annotation { "Feature Type Name" : "Feature", "Feature Type Description" : "" }
export const myFeature = defineFeature(function(context is Context, id is Id, definition is map)
    precondition{}
    {
        {
            var Q0;
            Q0=qCreatedBy(makeId("Top.planeOp"),FACE);
            var sketch = newSketch(context, id + "F0", { "sketchPlane" : qUnion([Q0])});
            skLineSegment(sketch, "E0", {"start": v(0, 0) * mm, "end": v(-38.42, 0) * mm});
            skLineSegment(sketch, "E1", {"start": v(-38.42, 0) * mm, "end": v(-32.56, -66.93) * mm});
            skLineSegment(sketch, "E2", {"start": v(-22.44, -76.2) * mm, "end": v(0, -76.2) * mm});
            skLineSegment(sketch, "E3", {"start": v(0, -76.2) * mm, "end": v(0, 0) * mm});
            skPoint(sketch, "E4.visualSharp", {"position": v(-31.75, -76.2) * mm});
            skArc(sketch, "E4.filletArc", {"start": v(-32.56, -66.93) * mm, "mid": v(-29.3, -73.53) * mm, "end": v(-22.44, -76.2) * mm});
            skSolve(sketch);
        }
        {
            var Q0;
            Q0=makeQuery(id+"F0.imprint","IMPRINT",FACE,{"disambiguationData":[TD([[makeQuery(id+"F0.imprint","IMPRINT",EDGE,{"derivedFrom":sQuery(id+"F0.wireOp",EDGE,"E0")}),1.0]])]});
            var Q1;
            Q1=sQuery(id+"F0.wireOp",EDGE,"E3");
            revolve(context, id + "F1", {"surfaceOperationType" : NewSurfaceOperationType.NEW, "entities" : qUnion([Q0]), "axis" : qUnion([Q1]), "revolveType" : RevolveType.FULL});
        }
        {
            var Q0;
            Q0=makeQuery(id+"F1.opRevolve","SWEPT_EDGE",EDGE,{"disambiguationData":[OSD([sQuery(id+"F0.wireOp",EDGE,"E0"),sQuery(id+"F0.wireOp",EDGE,"E1")])]});
            var Q1;
            Q1=makeQuery(id+"F3.opShell","OFFSET_EDGE",EDGE,{"disambiguationData":[OSD([sQuery(id+"F0.wireOp",EDGE,"E0"),sQuery(id+"F0.wireOp",EDGE,"E1")])]});
            fillet(context, id + "F2", {"entities" : qUnion([Q0, Q1]), "radius" : 1.27 * mm, "tangentPropagation" : true, "allowEdgeOverflow" : false});
        }
        {
            var Q0;
            Q0=makeQuery(id+"F1.opRevolve","SWEPT_FACE",FACE,{"disambiguationData":[OSD([sQuery(id+"F0.wireOp",EDGE,"E0")])]});
            shell(context, id + "F3", {"entities" : qUnion([Q0]), "thickness" : 2.54 * mm});
        }
        {
            var Q0;
            Q0=qCreatedBy(makeId("Top.planeOp"),FACE);
            var sketch = newSketch(context, id + "F4", { "sketchPlane" : qUnion([Q0])});
            skArc(sketch, "E5", {"start": v(-13.78, -14.23) * mm, "mid": v(-23.6, -20.04) * mm, "end": v(-13.78, -25.85) * mm});
            skArc(sketch, "E6", {"start": v(-12.2, -12.87) * mm, "mid": v(-25.58, -20.04) * mm, "end": v(-12.2, -27.2) * mm});
            skArc(sketch, "E7", {"start": v(-12.2, -15.44) * mm, "mid": v(-14.05, -20.04) * mm, "end": v(-12.2, -24.64) * mm});
            skArc(sketch, "E8", {"start": v(-13.78, -14.23) * mm, "mid": v(-16.03, -20.04) * mm, "end": v(-13.78, -25.85) * mm});
            skArc(sketch, "E9", {"start": v(-1, -25.78) * mm, "mid": v(2.24, -26.67) * mm, "end": v(5.5, -25.85) * mm});
            skArc(sketch, "E10", {"start": v(-2.56, -27.14) * mm, "mid": v(2.25, -28.65) * mm, "end": v(7.08, -27.2) * mm});
            skArc(sketch, "E11", {"start": v(7.08, -15.44) * mm, "mid": v(5.23, -20.04) * mm, "end": v(7.08, -24.64) * mm});
            skArc(sketch, "E12", {"start": v(5.5, -14.23) * mm, "mid": v(3.25, -20.04) * mm, "end": v(5.5, -25.85) * mm});
            skArc(sketch, "E13.trimOffspring", {"start": v(-12.2, -24.64) * mm, "mid": v(-10.34, -20.04) * mm, "end": v(-12.2, -15.44) * mm});
            skArc(sketch, "E14.trimOffspring", {"start": v(-10.62, -25.85) * mm, "mid": v(-7.35, -26.67) * mm, "end": v(-4.1, -25.78) * mm});
            skArc(sketch, "E15.trimOffspring", {"start": v(-12.2, -27.2) * mm, "mid": v(-7.37, -28.65) * mm, "end": v(-2.56, -27.14) * mm});
            skArc(sketch, "E16.trimOffspring", {"start": v(-10.62, -25.85) * mm, "mid": v(-8.36, -20.04) * mm, "end": v(-10.62, -14.23) * mm});
            skArc(sketch, "E17.trimOffspring", {"start": v(-2.56, -24.54) * mm, "mid": v(-0.8, -20.04) * mm, "end": v(-2.56, -15.53) * mm});
            skArc(sketch, "E18.trimOffspring", {"start": v(-1, -25.78) * mm, "mid": v(1.19, -20.04) * mm, "end": v(-1, -14.3) * mm});
            skArc(sketch, "E19.trimOffspring", {"start": v(-4.1, -14.3) * mm, "mid": v(-6.3, -20.04) * mm, "end": v(-4.1, -25.78) * mm});
            skArc(sketch, "E20.trimOffspring", {"start": v(-4.1, -14.3) * mm, "mid": v(-7.35, -13.4) * mm, "end": v(-10.62, -14.23) * mm});
            skArc(sketch, "E21.trimOffspring", {"start": v(-2.56, -15.53) * mm, "mid": v(-4.32, -20.04) * mm, "end": v(-2.56, -24.54) * mm});
            skArc(sketch, "E22.trimOffspring", {"start": v(-2.56, -12.93) * mm, "mid": v(-7.37, -11.43) * mm, "end": v(-12.2, -12.87) * mm});
            skArc(sketch, "E23.trimOffspring", {"start": v(5.5, -14.23) * mm, "mid": v(2.24, -13.4) * mm, "end": v(-1, -14.3) * mm});
            skArc(sketch, "E24.trimOffspring", {"start": v(7.08, -12.87) * mm, "mid": v(2.25, -11.43) * mm, "end": v(-2.56, -12.93) * mm});
            skArc(sketch, "E25.trimOffspring", {"start": v(8.66, -25.85) * mm, "mid": v(18.49, -20.04) * mm, "end": v(8.66, -14.23) * mm});
            skArc(sketch, "E26.trimOffspring", {"start": v(7.08, -24.64) * mm, "mid": v(8.94, -20.04) * mm, "end": v(7.08, -15.44) * mm});
            skArc(sketch, "E27.trimOffspring", {"start": v(8.66, -25.85) * mm, "mid": v(10.92, -20.04) * mm, "end": v(8.66, -14.23) * mm});
            skArc(sketch, "E28.trimOffspring", {"start": v(7.08, -27.2) * mm, "mid": v(20.47, -20.04) * mm, "end": v(7.08, -12.87) * mm});
            skSolve(sketch);
        }
        {
            var Q0;
            Q0=makeQuery(id+"F4.imprint","IMPRINT",FACE,{"disambiguationData":[TD([[makeQuery(id+"F4.imprint","IMPRINT",EDGE,{"derivedFrom":sQuery(id+"F4.wireOp",EDGE,"E5")}),-1.0]])]});
            var Q1;
            Q1=sQuery(id+"F4.wireOp",EDGE,"E6");
            var Q2;
            Q2=sQuery(id+"F4.wireOp",EDGE,"E5");
            var Q3;
            Q3=sQuery(id+"F4.wireOp",EDGE,"E8");
            var Q4;
            Q4=sQuery(id+"F4.wireOp",EDGE,"E7");
            var Q5;
            Q5=sQuery(id+"F4.wireOp",EDGE,"E13.trimOffspring");
            var Q6;
            Q6=sQuery(id+"F4.wireOp",EDGE,"E16.trimOffspring");
            var Q7;
            Q7=sQuery(id+"F4.wireOp",EDGE,"E20.trimOffspring");
            var Q8;
            Q8=sQuery(id+"F4.wireOp",EDGE,"E22.trimOffspring");
            var Q9;
            Q9=sQuery(id+"F4.wireOp",EDGE,"E19.trimOffspring");
            var Q10;
            Q10=sQuery(id+"F4.wireOp",EDGE,"E21.trimOffspring");
            var Q11;
            Q11=sQuery(id+"F4.wireOp",EDGE,"E14.trimOffspring");
            var Q12;
            Q12=sQuery(id+"F4.wireOp",EDGE,"E15.trimOffspring");
            var Q13;
            Q13=sQuery(id+"F4.wireOp",EDGE,"E10");
            var Q14;
            Q14=sQuery(id+"F4.wireOp",EDGE,"E9");
            var Q15;
            Q15=sQuery(id+"F4.wireOp",EDGE,"E18.trimOffspring");
            var Q16;
            Q16=sQuery(id+"F4.wireOp",EDGE,"E17.trimOffspring");
            var Q17;
            Q17=sQuery(id+"F4.wireOp",EDGE,"E23.trimOffspring");
            var Q18;
            Q18=sQuery(id+"F4.wireOp",EDGE,"E24.trimOffspring");
            var Q19;
            Q19=sQuery(id+"F4.wireOp",EDGE,"E12");
            var Q20;
            Q20=sQuery(id+"F4.wireOp",EDGE,"E11");
            var Q21;
            Q21=sQuery(id+"F4.wireOp",EDGE,"E26.trimOffspring");
            var Q22;
            Q22=sQuery(id+"F4.wireOp",EDGE,"E27.trimOffspring");
            var Q23;
            Q23=sQuery(id+"F4.wireOp",EDGE,"E25.trimOffspring");
            var Q24;
            Q24=sQuery(id+"F4.wireOp",EDGE,"E28.trimOffspring");
            extrude(context, id + "F5", {"entities" : qUnion([Q0]), "operationType" : NewBodyOperationType.ADD, "surfaceOperationType" : NewSurfaceOperationType.ADD, "surfaceEntities" : qUnion([Q1, Q2, Q3, Q4, Q5, Q6, Q7, Q8, Q9, Q10, Q11, Q12, Q13, Q14, Q15, Q16, Q17, Q18, Q19, Q20, Q21, Q22, Q23, Q24]), "endBound" : BoundingType.UP_TO_NEXT, "depth" : 25.4 * mm, "hasOffset" : true, "offsetDistance" : 5.08 * mm, "offsetOppositeDirection" : true});
        }
        {
            var Q0;
            Q0=makeQuery(id+"F5.opExtrude","CAP_FACE",FACE,{"disambiguationData":[OSD([sQuery(id+"F4.wireOp",EDGE,"E5"),sQuery(id+"F4.wireOp",EDGE,"E6"),sQuery(id+"F4.wireOp",EDGE,"E7"),sQuery(id+"F4.wireOp",EDGE,"E8"),sQuery(id+"F4.wireOp",EDGE,"E9"),sQuery(id+"F4.wireOp",EDGE,"E10"),sQuery(id+"F4.wireOp",EDGE,"E11"),sQuery(id+"F4.wireOp",EDGE,"E12"),sQuery(id+"F4.wireOp",EDGE,"E13.trimOffspring"),sQuery(id+"F4.wireOp",EDGE,"E14.trimOffspring"),sQuery(id+"F4.wireOp",EDGE,"E15.trimOffspring"),sQuery(id+"F4.wireOp",EDGE,"E16.trimOffspring"),sQuery(id+"F4.wireOp",EDGE,"E17.trimOffspring"),sQuery(id+"F4.wireOp",EDGE,"E18.trimOffspring"),sQuery(id+"F4.wireOp",EDGE,"E19.trimOffspring"),sQuery(id+"F4.wireOp",EDGE,"E20.trimOffspring"),sQuery(id+"F4.wireOp",EDGE,"E21.trimOffspring"),sQuery(id+"F4.wireOp",EDGE,"E22.trimOffspring"),sQuery(id+"F4.wireOp",EDGE,"E23.trimOffspring"),sQuery(id+"F4.wireOp",EDGE,"E24.trimOffspring"),sQuery(id+"F4.wireOp",EDGE,"E25.trimOffspring"),sQuery(id+"F4.wireOp",EDGE,"E26.trimOffspring"),sQuery(id+"F4.wireOp",EDGE,"E27.trimOffspring"),sQuery(id+"F4.wireOp",EDGE,"E28.trimOffspring")])],"isStart":true});
            var Q1;
            Q1=makeQuery(id+"F5.boolean.opBoolean","SPLIT",FACE,{"disambiguationData":[TD([makeQuery(id+"F1.opRevolve","SWEPT_FACE",FACE,{"disambiguationData":[OSD([sQuery(id+"F0.wireOp",EDGE,"E0")])]})])],"derivedFrom":makeQuery(id+"F3.opShell","OFFSET_FACE",FACE,{"disambiguationData":[OSD([sQuery(id+"F0.wireOp",EDGE,"E1")])]})});
            extrude(context, id + "F6", {"entities" : qUnion([Q0]), "operationType" : NewBodyOperationType.REMOVE, "endBound" : BoundingType.UP_TO_SURFACE, "oppositeDirection" : true, "depth" : 25.4 * mm, "endBoundEntityFace" : qUnion([Q1]), "offsetDistance" : 25.4 * mm});
        }
        {
            var Q0;
            Q0=makeQuery(id+"F3.opShell","OFFSET_EDGE",EDGE,{"disambiguationData":[OSD([sQuery(id+"F0.wireOp",EDGE,"E0"),sQuery(id+"F0.wireOp",EDGE,"E1")])]});
            fillet(context, id + "F7", {"entities" : qUnion([Q0]), "radius" : 1.27 * mm, "tangentPropagation" : true, "allowEdgeOverflow" : false});
        }
        {
            var Q0;
            Q0=qCreatedBy(makeId("Top.planeOp"),FACE);
            var sketch = newSketch(context, id + "F8", { "sketchPlane" : qUnion([Q0])});
            skText(sketch, "E29", { "text": "Roberto Fdez", "fontName": "OpenSans-Regular.ttf"});
            const initialGuessF8  = {"E29": [-0.0276, -0.0377, 1, 0, 0.00581]};
            skSetInitialGuess(sketch, initialGuessF8);
            skSolve(sketch);
        }
        {
            var Q0;
            Q0 = qSketchRegion(id + "F8", true);
            var Q1;
            {var subQ0=sQuery(id+"F0.wireOp",EDGE,"E1");Q1=makeQuery(id+"F5.boolean.opBoolean","SPLIT",FACE,{"disambiguationData":[TD([makeQuery(id+"F1.opRevolve","SWEPT_FACE",FACE,{"disambiguationData":[OSD([sQuery(id+"F0.wireOp",EDGE,"E4.filletArc")])]})])],"derivedFrom":makeQuery(id+"F1.opRevolve","SWEPT_FACE",FACE,{"disambiguationData":[OSD([subQ0])]})});}
            extrude(context, id + "F9", {"entities" : qUnion([Q0]), "operationType" : NewBodyOperationType.ADD, "endBound" : BoundingType.UP_TO_NEXT, "depth" : 25.4 * mm, "endBoundEntityFace" : qUnion([Q1]), "hasOffset" : true, "offsetDistance" : 5.08 * mm, "offsetOppositeDirection" : true});
        }
        {
            var Q0;
            Q0=makeQuery(id+"F9.opExtrude","CAP_FACE",FACE,{"disambiguationData":[OSD([sQuery(id+"F8.wireOp",EDGE,"E29.sketch_text.stroke-0"),sQuery(id+"F8.wireOp",EDGE,"E29.sketch_text.stroke-1"),sQuery(id+"F8.wireOp",EDGE,"E29.sketch_text.stroke-2"),sQuery(id+"F8.wireOp",EDGE,"E29.sketch_text.stroke-3"),sQuery(id+"F8.wireOp",EDGE,"E29.sketch_text.stroke-4"),sQuery(id+"F8.wireOp",EDGE,"E29.sketch_text.stroke-5"),sQuery(id+"F8.wireOp",EDGE,"E29.sketch_text.stroke-6"),sQuery(id+"F8.wireOp",EDGE,"E29.sketch_text.stroke-7"),sQuery(id+"F8.wireOp",EDGE,"E29.sketch_text.stroke-8"),sQuery(id+"F8.wireOp",EDGE,"E29.sketch_text.stroke-9"),sQuery(id+"F8.wireOp",EDGE,"E29.sketch_text.stroke-10"),sQuery(id+"F8.wireOp",EDGE,"E29.sketch_text.stroke-11"),sQuery(id+"F8.wireOp",EDGE,"E29.sketch_text.stroke-12"),sQuery(id+"F8.wireOp",EDGE,"E29.sketch_text.stroke-13"),sQuery(id+"F8.wireOp",EDGE,"E29.sketch_text.stroke-14"),sQuery(id+"F8.wireOp",EDGE,"E29.sketch_text.stroke-15"),sQuery(id+"F8.wireOp",EDGE,"E29.sketch_text.stroke-16"),sQuery(id+"F8.wireOp",EDGE,"E29.sketch_text.stroke-17")])],"isStart":true});
            var Q1;
            Q1=makeQuery(id+"F9.opExtrude","CAP_FACE",FACE,{"disambiguationData":[OSD([sQuery(id+"F8.wireOp",EDGE,"E29.sketch_text.stroke-18"),sQuery(id+"F8.wireOp",EDGE,"E29.sketch_text.stroke-19"),sQuery(id+"F8.wireOp",EDGE,"E29.sketch_text.stroke-20"),sQuery(id+"F8.wireOp",EDGE,"E29.sketch_text.stroke-21"),sQuery(id+"F8.wireOp",EDGE,"E29.sketch_text.stroke-22"),sQuery(id+"F8.wireOp",EDGE,"E29.sketch_text.stroke-23"),sQuery(id+"F8.wireOp",EDGE,"E29.sketch_text.stroke-24"),sQuery(id+"F8.wireOp",EDGE,"E29.sketch_text.stroke-25"),sQuery(id+"F8.wireOp",EDGE,"E29.sketch_text.stroke-26"),sQuery(id+"F8.wireOp",EDGE,"E29.sketch_text.stroke-27"),sQuery(id+"F8.wireOp",EDGE,"E29.sketch_text.stroke-28"),sQuery(id+"F8.wireOp",EDGE,"E29.sketch_text.stroke-29"),sQuery(id+"F8.wireOp",EDGE,"E29.sketch_text.stroke-30"),sQuery(id+"F8.wireOp",EDGE,"E29.sketch_text.stroke-31"),sQuery(id+"F8.wireOp",EDGE,"E29.sketch_text.stroke-32"),sQuery(id+"F8.wireOp",EDGE,"E29.sketch_text.stroke-33"),sQuery(id+"F8.wireOp",EDGE,"E29.sketch_text.stroke-34")])],"isStart":true});
            var Q2;
            Q2=makeQuery(id+"F9.opExtrude","CAP_FACE",FACE,{"disambiguationData":[OSD([sQuery(id+"F8.wireOp",EDGE,"E29.sketch_text.stroke-35"),sQuery(id+"F8.wireOp",EDGE,"E29.sketch_text.stroke-36"),sQuery(id+"F8.wireOp",EDGE,"E29.sketch_text.stroke-37"),sQuery(id+"F8.wireOp",EDGE,"E29.sketch_text.stroke-38"),sQuery(id+"F8.wireOp",EDGE,"E29.sketch_text.stroke-39"),sQuery(id+"F8.wireOp",EDGE,"E29.sketch_text.stroke-40"),sQuery(id+"F8.wireOp",EDGE,"E29.sketch_text.stroke-41"),sQuery(id+"F8.wireOp",EDGE,"E29.sketch_text.stroke-42"),sQuery(id+"F8.wireOp",EDGE,"E29.sketch_text.stroke-43"),sQuery(id+"F8.wireOp",EDGE,"E29.sketch_text.stroke-44"),sQuery(id+"F8.wireOp",EDGE,"E29.sketch_text.stroke-45"),sQuery(id+"F8.wireOp",EDGE,"E29.sketch_text.stroke-46"),sQuery(id+"F8.wireOp",EDGE,"E29.sketch_text.stroke-47"),sQuery(id+"F8.wireOp",EDGE,"E29.sketch_text.stroke-48"),sQuery(id+"F8.wireOp",EDGE,"E29.sketch_text.stroke-49"),sQuery(id+"F8.wireOp",EDGE,"E29.sketch_text.stroke-50"),sQuery(id+"F8.wireOp",EDGE,"E29.sketch_text.stroke-51"),sQuery(id+"F8.wireOp",EDGE,"E29.sketch_text.stroke-52"),sQuery(id+"F8.wireOp",EDGE,"E29.sketch_text.stroke-53"),sQuery(id+"F8.wireOp",EDGE,"E29.sketch_text.stroke-54"),sQuery(id+"F8.wireOp",EDGE,"E29.sketch_text.stroke-55"),sQuery(id+"F8.wireOp",EDGE,"E29.sketch_text.stroke-56"),sQuery(id+"F8.wireOp",EDGE,"E29.sketch_text.stroke-57")])],"isStart":true});
            var Q3;
            Q3=makeQuery(id+"F9.opExtrude","CAP_FACE",FACE,{"disambiguationData":[OSD([sQuery(id+"F8.wireOp",EDGE,"E29.sketch_text.stroke-58"),sQuery(id+"F8.wireOp",EDGE,"E29.sketch_text.stroke-59"),sQuery(id+"F8.wireOp",EDGE,"E29.sketch_text.stroke-60"),sQuery(id+"F8.wireOp",EDGE,"E29.sketch_text.stroke-61"),sQuery(id+"F8.wireOp",EDGE,"E29.sketch_text.stroke-62"),sQuery(id+"F8.wireOp",EDGE,"E29.sketch_text.stroke-63"),sQuery(id+"F8.wireOp",EDGE,"E29.sketch_text.stroke-64"),sQuery(id+"F8.wireOp",EDGE,"E29.sketch_text.stroke-65"),sQuery(id+"F8.wireOp",EDGE,"E29.sketch_text.stroke-66"),sQuery(id+"F8.wireOp",EDGE,"E29.sketch_text.stroke-67"),sQuery(id+"F8.wireOp",EDGE,"E29.sketch_text.stroke-68"),sQuery(id+"F8.wireOp",EDGE,"E29.sketch_text.stroke-69"),sQuery(id+"F8.wireOp",EDGE,"E29.sketch_text.stroke-70"),sQuery(id+"F8.wireOp",EDGE,"E29.sketch_text.stroke-71"),sQuery(id+"F8.wireOp",EDGE,"E29.sketch_text.stroke-72"),sQuery(id+"F8.wireOp",EDGE,"E29.sketch_text.stroke-73"),sQuery(id+"F8.wireOp",EDGE,"E29.sketch_text.stroke-74"),sQuery(id+"F8.wireOp",EDGE,"E29.sketch_text.stroke-75"),sQuery(id+"F8.wireOp",EDGE,"E29.sketch_text.stroke-76")])],"isStart":true});
            var Q4;
            Q4=makeQuery(id+"F9.opExtrude","CAP_FACE",FACE,{"disambiguationData":[OSD([sQuery(id+"F8.wireOp",EDGE,"E29.sketch_text.stroke-77"),sQuery(id+"F8.wireOp",EDGE,"E29.sketch_text.stroke-78"),sQuery(id+"F8.wireOp",EDGE,"E29.sketch_text.stroke-79"),sQuery(id+"F8.wireOp",EDGE,"E29.sketch_text.stroke-80"),sQuery(id+"F8.wireOp",EDGE,"E29.sketch_text.stroke-81"),sQuery(id+"F8.wireOp",EDGE,"E29.sketch_text.stroke-82"),sQuery(id+"F8.wireOp",EDGE,"E29.sketch_text.stroke-83"),sQuery(id+"F8.wireOp",EDGE,"E29.sketch_text.stroke-84"),sQuery(id+"F8.wireOp",EDGE,"E29.sketch_text.stroke-85"),sQuery(id+"F8.wireOp",EDGE,"E29.sketch_text.stroke-86"),sQuery(id+"F8.wireOp",EDGE,"E29.sketch_text.stroke-87"),sQuery(id+"F8.wireOp",EDGE,"E29.sketch_text.stroke-88"),sQuery(id+"F8.wireOp",EDGE,"E29.sketch_text.stroke-89")])],"isStart":true});
            var Q5;
            Q5=makeQuery(id+"F9.opExtrude","CAP_FACE",FACE,{"disambiguationData":[OSD([sQuery(id+"F8.wireOp",EDGE,"E29.sketch_text.stroke-90"),sQuery(id+"F8.wireOp",EDGE,"E29.sketch_text.stroke-91"),sQuery(id+"F8.wireOp",EDGE,"E29.sketch_text.stroke-92"),sQuery(id+"F8.wireOp",EDGE,"E29.sketch_text.stroke-93"),sQuery(id+"F8.wireOp",EDGE,"E29.sketch_text.stroke-94"),sQuery(id+"F8.wireOp",EDGE,"E29.sketch_text.stroke-95"),sQuery(id+"F8.wireOp",EDGE,"E29.sketch_text.stroke-96"),sQuery(id+"F8.wireOp",EDGE,"E29.sketch_text.stroke-97"),sQuery(id+"F8.wireOp",EDGE,"E29.sketch_text.stroke-98"),sQuery(id+"F8.wireOp",EDGE,"E29.sketch_text.stroke-99"),sQuery(id+"F8.wireOp",EDGE,"E29.sketch_text.stroke-100"),sQuery(id+"F8.wireOp",EDGE,"E29.sketch_text.stroke-101"),sQuery(id+"F8.wireOp",EDGE,"E29.sketch_text.stroke-102"),sQuery(id+"F8.wireOp",EDGE,"E29.sketch_text.stroke-103"),sQuery(id+"F8.wireOp",EDGE,"E29.sketch_text.stroke-104"),sQuery(id+"F8.wireOp",EDGE,"E29.sketch_text.stroke-105"),sQuery(id+"F8.wireOp",EDGE,"E29.sketch_text.stroke-106"),sQuery(id+"F8.wireOp",EDGE,"E29.sketch_text.stroke-107"),sQuery(id+"F8.wireOp",EDGE,"E29.sketch_text.stroke-108")])],"isStart":true});
            var Q6;
            Q6=makeQuery(id+"F9.opExtrude","CAP_FACE",FACE,{"disambiguationData":[OSD([sQuery(id+"F8.wireOp",EDGE,"E29.sketch_text.stroke-109"),sQuery(id+"F8.wireOp",EDGE,"E29.sketch_text.stroke-110"),sQuery(id+"F8.wireOp",EDGE,"E29.sketch_text.stroke-111"),sQuery(id+"F8.wireOp",EDGE,"E29.sketch_text.stroke-112"),sQuery(id+"F8.wireOp",EDGE,"E29.sketch_text.stroke-113"),sQuery(id+"F8.wireOp",EDGE,"E29.sketch_text.stroke-114"),sQuery(id+"F8.wireOp",EDGE,"E29.sketch_text.stroke-115"),sQuery(id+"F8.wireOp",EDGE,"E29.sketch_text.stroke-116"),sQuery(id+"F8.wireOp",EDGE,"E29.sketch_text.stroke-117"),sQuery(id+"F8.wireOp",EDGE,"E29.sketch_text.stroke-118"),sQuery(id+"F8.wireOp",EDGE,"E29.sketch_text.stroke-119"),sQuery(id+"F8.wireOp",EDGE,"E29.sketch_text.stroke-120"),sQuery(id+"F8.wireOp",EDGE,"E29.sketch_text.stroke-121"),sQuery(id+"F8.wireOp",EDGE,"E29.sketch_text.stroke-122"),sQuery(id+"F8.wireOp",EDGE,"E29.sketch_text.stroke-123"),sQuery(id+"F8.wireOp",EDGE,"E29.sketch_text.stroke-124"),sQuery(id+"F8.wireOp",EDGE,"E29.sketch_text.stroke-125")])],"isStart":true});
            var Q7;
            Q7=makeQuery(id+"F9.opExtrude","CAP_FACE",FACE,{"disambiguationData":[OSD([sQuery(id+"F8.wireOp",EDGE,"E29.sketch_text.stroke-126"),sQuery(id+"F8.wireOp",EDGE,"E29.sketch_text.stroke-127"),sQuery(id+"F8.wireOp",EDGE,"E29.sketch_text.stroke-128"),sQuery(id+"F8.wireOp",EDGE,"E29.sketch_text.stroke-129"),sQuery(id+"F8.wireOp",EDGE,"E29.sketch_text.stroke-130"),sQuery(id+"F8.wireOp",EDGE,"E29.sketch_text.stroke-131"),sQuery(id+"F8.wireOp",EDGE,"E29.sketch_text.stroke-132"),sQuery(id+"F8.wireOp",EDGE,"E29.sketch_text.stroke-133"),sQuery(id+"F8.wireOp",EDGE,"E29.sketch_text.stroke-134"),sQuery(id+"F8.wireOp",EDGE,"E29.sketch_text.stroke-135")])],"isStart":true});
            var Q8;
            Q8=makeQuery(id+"F9.opExtrude","CAP_FACE",FACE,{"disambiguationData":[OSD([sQuery(id+"F8.wireOp",EDGE,"E29.sketch_text.stroke-136"),sQuery(id+"F8.wireOp",EDGE,"E29.sketch_text.stroke-137"),sQuery(id+"F8.wireOp",EDGE,"E29.sketch_text.stroke-138"),sQuery(id+"F8.wireOp",EDGE,"E29.sketch_text.stroke-139"),sQuery(id+"F8.wireOp",EDGE,"E29.sketch_text.stroke-140"),sQuery(id+"F8.wireOp",EDGE,"E29.sketch_text.stroke-141"),sQuery(id+"F8.wireOp",EDGE,"E29.sketch_text.stroke-142"),sQuery(id+"F8.wireOp",EDGE,"E29.sketch_text.stroke-143"),sQuery(id+"F8.wireOp",EDGE,"E29.sketch_text.stroke-144"),sQuery(id+"F8.wireOp",EDGE,"E29.sketch_text.stroke-145"),sQuery(id+"F8.wireOp",EDGE,"E29.sketch_text.stroke-146"),sQuery(id+"F8.wireOp",EDGE,"E29.sketch_text.stroke-147"),sQuery(id+"F8.wireOp",EDGE,"E29.sketch_text.stroke-148"),sQuery(id+"F8.wireOp",EDGE,"E29.sketch_text.stroke-149"),sQuery(id+"F8.wireOp",EDGE,"E29.sketch_text.stroke-150"),sQuery(id+"F8.wireOp",EDGE,"E29.sketch_text.stroke-151"),sQuery(id+"F8.wireOp",EDGE,"E29.sketch_text.stroke-152"),sQuery(id+"F8.wireOp",EDGE,"E29.sketch_text.stroke-153"),sQuery(id+"F8.wireOp",EDGE,"E29.sketch_text.stroke-154"),sQuery(id+"F8.wireOp",EDGE,"E29.sketch_text.stroke-155"),sQuery(id+"F8.wireOp",EDGE,"E29.sketch_text.stroke-156"),sQuery(id+"F8.wireOp",EDGE,"E29.sketch_text.stroke-157"),sQuery(id+"F8.wireOp",EDGE,"E29.sketch_text.stroke-158"),sQuery(id+"F8.wireOp",EDGE,"E29.sketch_text.stroke-159")])],"isStart":true});
            var Q9;
            Q9=makeQuery(id+"F9.opExtrude","CAP_FACE",FACE,{"disambiguationData":[OSD([sQuery(id+"F8.wireOp",EDGE,"E29.sketch_text.stroke-160"),sQuery(id+"F8.wireOp",EDGE,"E29.sketch_text.stroke-161"),sQuery(id+"F8.wireOp",EDGE,"E29.sketch_text.stroke-162"),sQuery(id+"F8.wireOp",EDGE,"E29.sketch_text.stroke-163"),sQuery(id+"F8.wireOp",EDGE,"E29.sketch_text.stroke-164"),sQuery(id+"F8.wireOp",EDGE,"E29.sketch_text.stroke-165"),sQuery(id+"F8.wireOp",EDGE,"E29.sketch_text.stroke-166"),sQuery(id+"F8.wireOp",EDGE,"E29.sketch_text.stroke-167"),sQuery(id+"F8.wireOp",EDGE,"E29.sketch_text.stroke-168"),sQuery(id+"F8.wireOp",EDGE,"E29.sketch_text.stroke-169"),sQuery(id+"F8.wireOp",EDGE,"E29.sketch_text.stroke-170"),sQuery(id+"F8.wireOp",EDGE,"E29.sketch_text.stroke-171"),sQuery(id+"F8.wireOp",EDGE,"E29.sketch_text.stroke-172"),sQuery(id+"F8.wireOp",EDGE,"E29.sketch_text.stroke-173"),sQuery(id+"F8.wireOp",EDGE,"E29.sketch_text.stroke-174"),sQuery(id+"F8.wireOp",EDGE,"E29.sketch_text.stroke-175"),sQuery(id+"F8.wireOp",EDGE,"E29.sketch_text.stroke-176"),sQuery(id+"F8.wireOp",EDGE,"E29.sketch_text.stroke-177"),sQuery(id+"F8.wireOp",EDGE,"E29.sketch_text.stroke-178")])],"isStart":true});
            var Q10;
            Q10=makeQuery(id+"F9.opExtrude","CAP_FACE",FACE,{"disambiguationData":[OSD([sQuery(id+"F8.wireOp",EDGE,"E29.sketch_text.stroke-179"),sQuery(id+"F8.wireOp",EDGE,"E29.sketch_text.stroke-180"),sQuery(id+"F8.wireOp",EDGE,"E29.sketch_text.stroke-181"),sQuery(id+"F8.wireOp",EDGE,"E29.sketch_text.stroke-182"),sQuery(id+"F8.wireOp",EDGE,"E29.sketch_text.stroke-183"),sQuery(id+"F8.wireOp",EDGE,"E29.sketch_text.stroke-184"),sQuery(id+"F8.wireOp",EDGE,"E29.sketch_text.stroke-185"),sQuery(id+"F8.wireOp",EDGE,"E29.sketch_text.stroke-186"),sQuery(id+"F8.wireOp",EDGE,"E29.sketch_text.stroke-187"),sQuery(id+"F8.wireOp",EDGE,"E29.sketch_text.stroke-188")])],"isStart":true});
            var Q11;
            {var subQ0=makeQuery(id+"F3.opShell","OFFSET_FACE",FACE,{"disambiguationData":[OSD([sQuery(id+"F0.wireOp",EDGE,"E4.filletArc")])]});var subQ1=sQuery(id+"F0.wireOp",EDGE,"E1");var subQ2=sQuery(id+"F0.wireOp",EDGE,"E0");var subQ3=sQuery(id+"F4.wireOp",EDGE,"E28.trimOffspring");var subQ4=sQuery(id+"F4.wireOp",EDGE,"E27.trimOffspring");var subQ5=sQuery(id+"F4.wireOp",EDGE,"E26.trimOffspring");var subQ6=sQuery(id+"F4.wireOp",EDGE,"E25.trimOffspring");var subQ7=sQuery(id+"F4.wireOp",EDGE,"E24.trimOffspring");var subQ8=sQuery(id+"F4.wireOp",EDGE,"E23.trimOffspring");var subQ9=sQuery(id+"F4.wireOp",EDGE,"E22.trimOffspring");var subQ10=sQuery(id+"F4.wireOp",EDGE,"E21.trimOffspring");var subQ11=sQuery(id+"F4.wireOp",EDGE,"E20.trimOffspring");var subQ12=sQuery(id+"F4.wireOp",EDGE,"E19.trimOffspring");var subQ13=sQuery(id+"F4.wireOp",EDGE,"E18.trimOffspring");var subQ14=sQuery(id+"F4.wireOp",EDGE,"E17.trimOffspring");var subQ15=sQuery(id+"F4.wireOp",EDGE,"E16.trimOffspring");var subQ16=sQuery(id+"F4.wireOp",EDGE,"E15.trimOffspring");var subQ17=sQuery(id+"F4.wireOp",EDGE,"E14.trimOffspring");var subQ18=sQuery(id+"F4.wireOp",EDGE,"E13.trimOffspring");var subQ19=sQuery(id+"F4.wireOp",EDGE,"E12");var subQ20=sQuery(id+"F4.wireOp",EDGE,"E11");var subQ21=sQuery(id+"F4.wireOp",EDGE,"E10");var subQ22=sQuery(id+"F4.wireOp",EDGE,"E9");var subQ23=sQuery(id+"F4.wireOp",EDGE,"E8");var subQ24=sQuery(id+"F4.wireOp",EDGE,"E7");var subQ25=sQuery(id+"F4.wireOp",EDGE,"E6");var subQ26=sQuery(id+"F4.wireOp",EDGE,"E5");var subQ27=makeQuery(id+"F3.opShell","OFFSET_FACE",FACE,{"disambiguationData":[OSD([subQ1])]});Q11=makeQuery(id+"F9.boolean.opBoolean","SPLIT",FACE,{"disambiguationData":[TD([subQ0])],"derivedFrom":makeQuery(id+"F6.boolean.opBoolean","MERGE",FACE,{"derivedFrom":[makeQuery(id+"F5.boolean.opBoolean","SPLIT",FACE,{"disambiguationData":[TD([makeQuery(id+"F1.opRevolve","SWEPT_FACE",FACE,{"disambiguationData":[OSD([subQ2])]})])],"derivedFrom":subQ27}),makeQuery(id+"F5.boolean.opBoolean","SPLIT",FACE,{"disambiguationData":[TD([makeQuery(id+"F5.opExtrude","SWEPT_FACE",FACE,{"disambiguationData":[OSD([subQ26])]})])],"derivedFrom":subQ27}),makeQuery(id+"F5.boolean.opBoolean","SPLIT",FACE,{"disambiguationData":[TD([makeQuery(id+"F5.opExtrude","SWEPT_FACE",FACE,{"disambiguationData":[OSD([subQ24])]})])],"derivedFrom":subQ27}),makeQuery(id+"F5.boolean.opBoolean","SPLIT",FACE,{"disambiguationData":[TD([makeQuery(id+"F5.opExtrude","SWEPT_FACE",FACE,{"disambiguationData":[OSD([subQ20])]})])],"derivedFrom":subQ27}),makeQuery(id+"F5.boolean.opBoolean","SPLIT",FACE,{"disambiguationData":[TD([makeQuery(id+"F5.opExtrude","SWEPT_FACE",FACE,{"disambiguationData":[OSD([subQ14])]})])],"derivedFrom":subQ27}),makeQuery(id+"F5.boolean.opBoolean","SPLIT",FACE,{"disambiguationData":[TD([makeQuery(id+"F5.opExtrude","SWEPT_FACE",FACE,{"disambiguationData":[OSD([subQ6])]})])],"derivedFrom":subQ27}),makeQuery(id+"F5.boolean.opBoolean","SPLIT",FACE,{"disambiguationData":[TD([makeQuery(id+"F5.opExtrude","SWEPT_FACE",FACE,{"disambiguationData":[OSD([subQ22])]})])],"derivedFrom":subQ27}),makeQuery(id+"F5.boolean.opBoolean","SPLIT",FACE,{"disambiguationData":[TD([makeQuery(id+"F5.opExtrude","SWEPT_FACE",FACE,{"disambiguationData":[OSD([subQ17])]})])],"derivedFrom":subQ27})],"fromTools":[makeQuery(id+"F6.opExtrude","CAP_FACE",FACE,{"disambiguationData":[OSD([subQ26,subQ25,subQ24,subQ23,subQ22,subQ21,subQ20,subQ19,subQ18,subQ17,subQ16,subQ15,subQ14,subQ13,subQ12,subQ11,subQ10,subQ9,subQ8,subQ7,subQ6,subQ5,subQ4,subQ3])],"isStart":false})]})});}
            extrude(context, id + "F10", {"entities" : qUnion([Q0, Q1, Q2, Q3, Q4, Q5, Q6, Q7, Q8, Q9, Q10]), "operationType" : NewBodyOperationType.REMOVE, "endBound" : BoundingType.UP_TO_SURFACE, "oppositeDirection" : true, "depth" : 25.4 * mm, "endBoundEntityFace" : qUnion([Q11]), "offsetDistance" : 25.4 * mm});
        }
    });